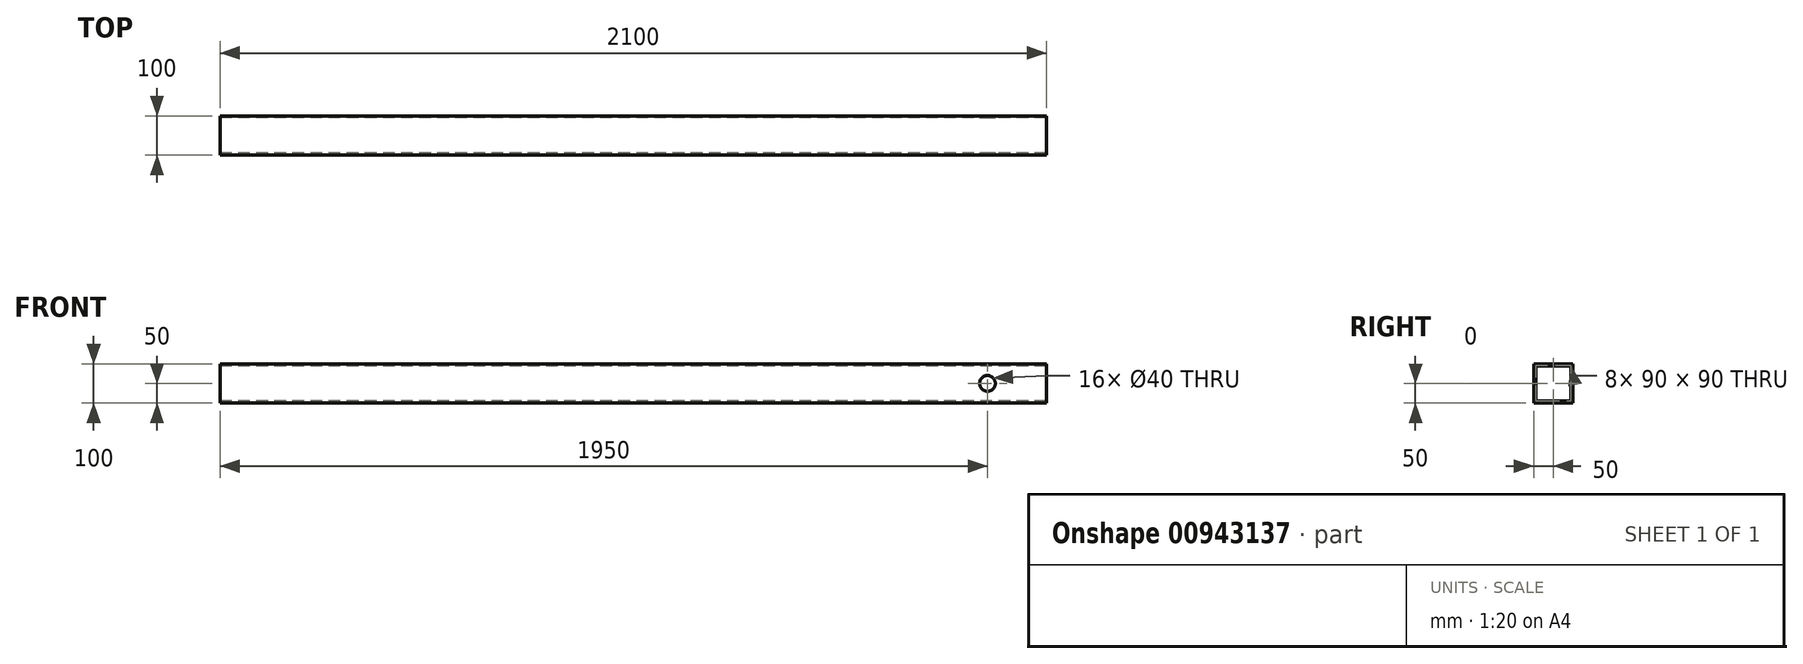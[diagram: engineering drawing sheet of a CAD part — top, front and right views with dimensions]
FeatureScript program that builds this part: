
annotation { "Feature Type Name" : "Feature", "Feature Type Description" : "" }
export const myFeature = defineFeature(function(context is Context, id is Id, definition is map)
    precondition{}
    {
        {
            var Q0;
            Q0=qCreatedBy(makeId("Right.planeOp"),FACE);
            var sketch = newSketch(context, id + "F0", { "sketchPlane" : qUnion([Q0])});
            skLineSegment(sketch, "E0.bottom", {"start": v(50, 50) * mm, "end": v(-50, 50) * mm});
            skLineSegment(sketch, "E0.top", {"start": v(50, -50) * mm, "end": v(-50, -50) * mm});
            skLineSegment(sketch, "E0.left", {"start": v(50, 50) * mm, "end": v(50, -50) * mm});
            skLineSegment(sketch, "E0.right", {"start": v(-50, 50) * mm, "end": v(-50, -50) * mm});
            skPoint(sketch, "E0.middle", {"position": v(0, 0) * mm});
            skLineSegment(sketch, "E1.bottom", {"start": v(-45, -45) * mm, "end": v(45, -45) * mm});
            skLineSegment(sketch, "E1.top", {"start": v(-45, 45) * mm, "end": v(45, 45) * mm});
            skLineSegment(sketch, "E1.left", {"start": v(-45, -45) * mm, "end": v(-45, 45) * mm});
            skLineSegment(sketch, "E1.right", {"start": v(45, -45) * mm, "end": v(45, 45) * mm});
            skSolve(sketch);
        }
        {
            var Q0;
            Q0 = qSketchRegion(id + "F0", true);
            extrude(context, id + "F1", {"entities" : qUnion([Q0]), "depth" : 2100 * mm, "offsetDistance" : 25 * mm});
        }
        {
            var Q0;
            Q0=makeQuery(id+"F1.opExtrude","SWEPT_FACE",FACE,{"disambiguationData":[OSD([sQuery(id+"F0.wireOp",EDGE,"E0.right")])]});
            var sketch = newSketch(context, id + "F2", { "sketchPlane" : qUnion([Q0])});
            skCircle(sketch, "E2", {"center": v(1950, 0) * mm, "radius": 20 * mm});
            skSolve(sketch);
        }
        {
            var Q0;
            Q0 = qSketchRegion(id + "F2", true);
            extrude(context, id + "F3", {"entities" : qUnion([Q0]), "operationType" : NewBodyOperationType.REMOVE, "oppositeDirection" : true, "depth" : 100 * mm, "offsetDistance" : 25 * mm});
        }
    });
